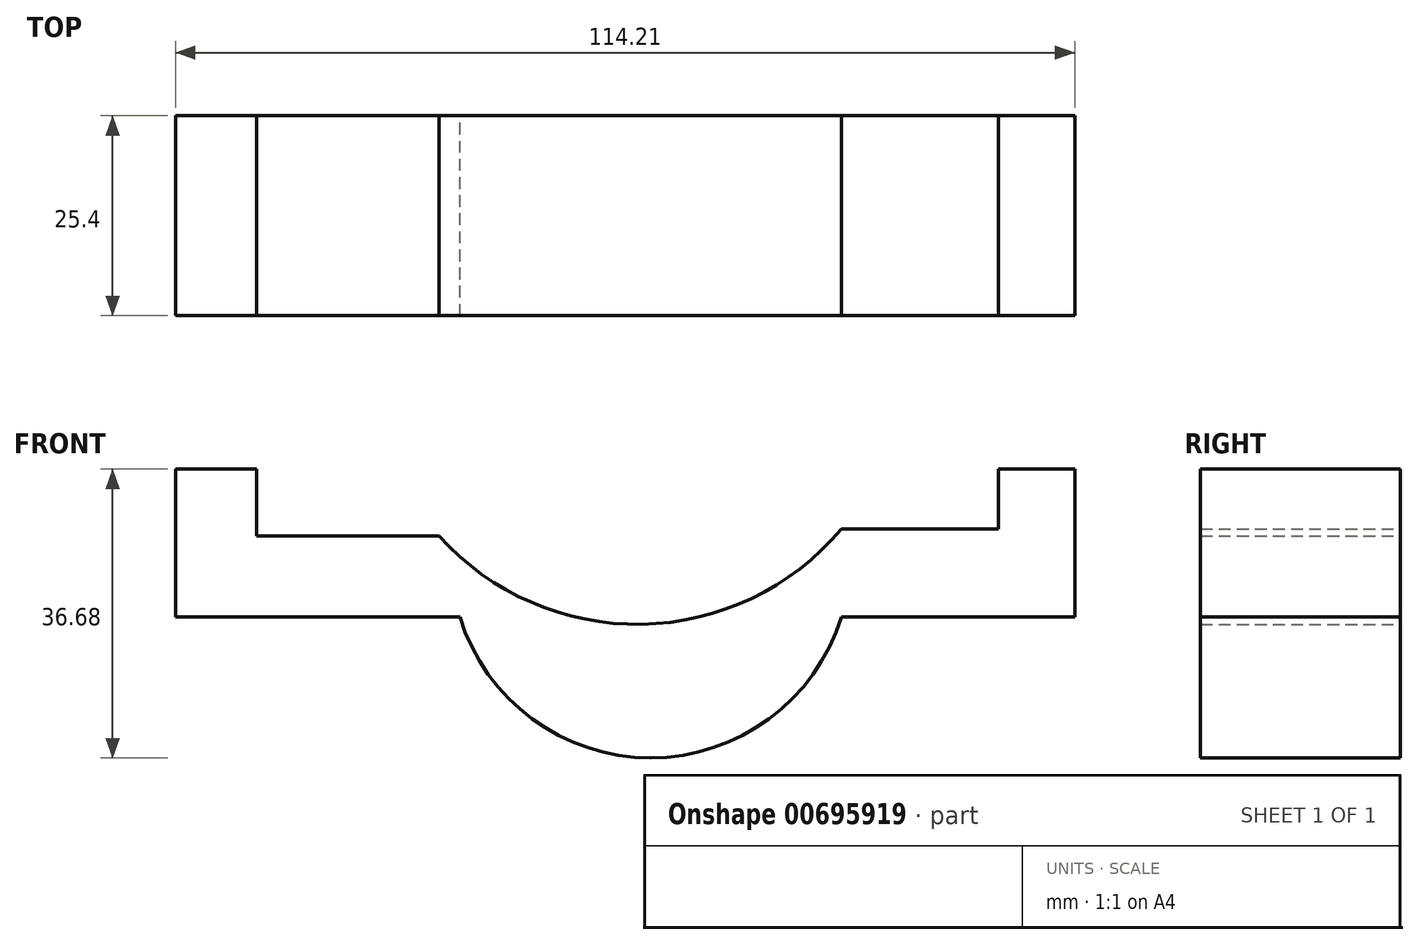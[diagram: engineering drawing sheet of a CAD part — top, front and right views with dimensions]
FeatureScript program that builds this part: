
annotation { "Feature Type Name" : "Feature", "Feature Type Description" : "" }
export const myFeature = defineFeature(function(context is Context, id is Id, definition is map)
    precondition{}
    {
        {
            var Q0;
            Q0=qCreatedBy(makeId("Front.planeOp"),FACE);
            var sketch = newSketch(context, id + "F0", { "sketchPlane" : qUnion([Q0])});
            skLineSegment(sketch, "E0", {"start": v(-76.2, 38.17) * mm, "end": v(-76.2, 19.38) * mm});
            skLineSegment(sketch, "E1", {"start": v(-76.2, 19.38) * mm, "end": v(-40.08, 19.38) * mm});
            skLineSegment(sketch, "E2", {"start": v(8.37, 19.38) * mm, "end": v(38.02, 19.38) * mm});
            skLineSegment(sketch, "E3", {"start": v(38.02, 19.38) * mm, "end": v(38.02, 38.17) * mm});
            skArc(sketch, "E4", {"start": v(-40.08, 19.38) * mm, "mid": v(-15.86, 1.49) * mm, "end": v(8.37, 19.38) * mm});
            skLineSegment(sketch, "E5", {"start": v(-76.2, 38.17) * mm, "end": v(-65.92, 38.17) * mm});
            skLineSegment(sketch, "E6", {"start": v(-65.92, 38.17) * mm, "end": v(-65.92, 29.66) * mm});
            skLineSegment(sketch, "E7", {"start": v(-65.92, 29.66) * mm, "end": v(-42.72, 29.66) * mm});
            skLineSegment(sketch, "E8", {"start": v(38.02, 38.17) * mm, "end": v(28.33, 38.17) * mm});
            skLineSegment(sketch, "E9", {"start": v(28.33, 38.17) * mm, "end": v(28.33, 30.54) * mm});
            skLineSegment(sketch, "E10", {"start": v(28.33, 30.54) * mm, "end": v(8.37, 30.54) * mm});
            skArc(sketch, "E11", {"start": v(-42.72, 29.66) * mm, "mid": v(-16.98, 18.46) * mm, "end": v(8.37, 30.54) * mm});
            skSolve(sketch);
        }
        {
            var Q0;
            Q0 = qSketchRegion(id + "F0", true);
            extrude(context, id + "F1", {"entities" : qUnion([Q0]), "depth" : 25.4 * mm, "offsetDistance" : 25.4 * mm});
        }
    });
